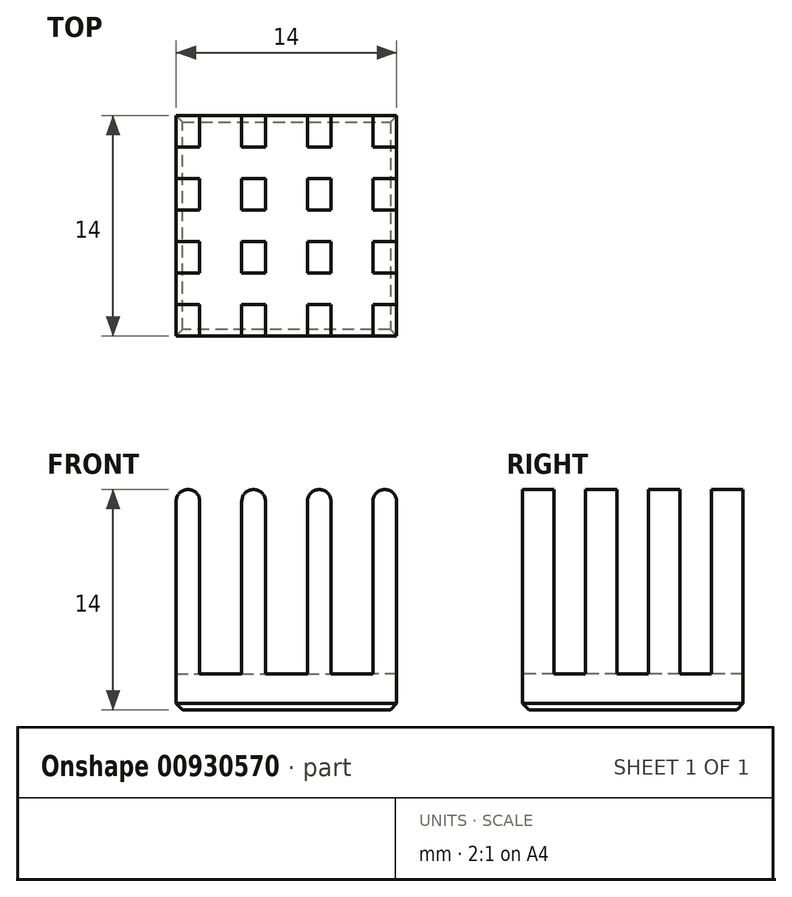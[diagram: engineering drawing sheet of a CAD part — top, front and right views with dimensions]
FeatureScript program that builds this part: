
annotation { "Feature Type Name" : "Feature", "Feature Type Description" : "" }
export const myFeature = defineFeature(function(context is Context, id is Id, definition is map)
    precondition{}
    {
        {
            var Q0;
            Q0=qCreatedBy(makeId("Top.planeOp"),FACE);
            var sketch = newSketch(context, id + "F0", { "sketchPlane" : qUnion([Q0])});
            skLineSegment(sketch, "E0.bottom", {"start": v(0, 0) * mm, "end": v(14, 0) * mm});
            skLineSegment(sketch, "E0.top", {"start": v(0, 14) * mm, "end": v(14, 14) * mm});
            skLineSegment(sketch, "E0.left", {"start": v(0, 0) * mm, "end": v(0, 14) * mm});
            skLineSegment(sketch, "E0.right", {"start": v(14, 0) * mm, "end": v(14, 14) * mm});
            skSolve(sketch);
        }
        {
            var Q0;
            Q0=qSketchRegion(id+"F0",true);
            extrude(context, id + "F1", {"entities" : qUnion([Q0]), "depth" : 2.3 * mm});
        }
        {
            var Q0;
            Q0=makeQuery(id+"F1.opExtrude","CAP_FACE",FACE,{"disambiguationData":[OSD([sQuery(id+"F0.wireOp",EDGE,"E0.bottom"),sQuery(id+"F0.wireOp",EDGE,"E0.top"),sQuery(id+"F0.wireOp",EDGE,"E0.left"),sQuery(id+"F0.wireOp",EDGE,"E0.right")])],"isStart":false});
            var sketch = newSketch(context, id + "F2", { "sketchPlane" : qUnion([Q0])});
            skLineSegment(sketch, "E1.bottom", {"start": v(0, 14) * mm, "end": v(1.5, 14) * mm});
            skLineSegment(sketch, "E1.top", {"start": v(0, 12) * mm, "end": v(1.5, 12) * mm});
            skLineSegment(sketch, "E1.left", {"start": v(0, 14) * mm, "end": v(0, 12) * mm});
            skLineSegment(sketch, "E1.right", {"start": v(1.5, 14) * mm, "end": v(1.5, 12) * mm});
            skLineSegment(sketch, "E2.bottom", {"start": v(0, 0) * mm, "end": v(1.5, 0) * mm});
            skLineSegment(sketch, "E2.top", {"start": v(0, 2) * mm, "end": v(1.5, 2) * mm});
            skLineSegment(sketch, "E2.left", {"start": v(0, 0) * mm, "end": v(0, 2) * mm});
            skLineSegment(sketch, "E2.right", {"start": v(1.5, 0) * mm, "end": v(1.5, 2) * mm});
            skLineSegment(sketch, "E3.bottom", {"start": v(14, 14) * mm, "end": v(12.5, 14) * mm});
            skLineSegment(sketch, "E3.top", {"start": v(14, 12) * mm, "end": v(12.5, 12) * mm});
            skLineSegment(sketch, "E3.left", {"start": v(14, 14) * mm, "end": v(14, 12) * mm});
            skLineSegment(sketch, "E3.right", {"start": v(12.5, 14) * mm, "end": v(12.5, 12) * mm});
            skLineSegment(sketch, "E4.bottom", {"start": v(14, 0) * mm, "end": v(12.5, 0) * mm});
            skLineSegment(sketch, "E4.top", {"start": v(14, 2) * mm, "end": v(12.5, 2) * mm});
            skLineSegment(sketch, "E4.left", {"start": v(14, 0) * mm, "end": v(14, 2) * mm});
            skLineSegment(sketch, "E4.right", {"start": v(12.5, 0) * mm, "end": v(12.5, 2) * mm});
            skLineSegment(sketch, "E5.bottom", {"start": v(0, 10) * mm, "end": v(1.5, 10) * mm});
            skLineSegment(sketch, "E5.top", {"start": v(0, 8) * mm, "end": v(1.5, 8) * mm});
            skLineSegment(sketch, "E5.left", {"start": v(0, 10) * mm, "end": v(0, 8) * mm});
            skLineSegment(sketch, "E5.right", {"start": v(1.5, 10) * mm, "end": v(1.5, 8) * mm});
            skLineSegment(sketch, "E6.bottom", {"start": v(0, 6) * mm, "end": v(1.5, 6) * mm});
            skLineSegment(sketch, "E6.top", {"start": v(0, 4) * mm, "end": v(1.5, 4) * mm});
            skLineSegment(sketch, "E6.left", {"start": v(0, 6) * mm, "end": v(0, 4) * mm});
            skLineSegment(sketch, "E6.right", {"start": v(1.5, 6) * mm, "end": v(1.5, 4) * mm});
            skLineSegment(sketch, "E7.bottom", {"start": v(14, 10) * mm, "end": v(12.5, 10) * mm});
            skLineSegment(sketch, "E7.top", {"start": v(14, 8) * mm, "end": v(12.5, 8) * mm});
            skLineSegment(sketch, "E7.left", {"start": v(14, 10) * mm, "end": v(14, 8) * mm});
            skLineSegment(sketch, "E7.right", {"start": v(12.5, 10) * mm, "end": v(12.5, 8) * mm});
            skLineSegment(sketch, "E8.bottom", {"start": v(14, 6) * mm, "end": v(12.5, 6) * mm});
            skLineSegment(sketch, "E8.top", {"start": v(14, 4) * mm, "end": v(12.5, 4) * mm});
            skLineSegment(sketch, "E8.left", {"start": v(14, 6) * mm, "end": v(14, 4) * mm});
            skLineSegment(sketch, "E8.right", {"start": v(12.5, 6) * mm, "end": v(12.5, 4) * mm});
            skLineSegment(sketch, "E9.bottom", {"start": v(4.17, 10) * mm, "end": v(5.67, 10) * mm});
            skLineSegment(sketch, "E9.top", {"start": v(4.17, 8) * mm, "end": v(5.67, 8) * mm});
            skLineSegment(sketch, "E9.left", {"start": v(4.17, 10) * mm, "end": v(4.17, 8) * mm});
            skLineSegment(sketch, "E9.right", {"start": v(5.67, 10) * mm, "end": v(5.67, 8) * mm});
            skLineSegment(sketch, "E10.bottom", {"start": v(8.33, 10) * mm, "end": v(9.83, 10) * mm});
            skLineSegment(sketch, "E10.top", {"start": v(8.33, 8) * mm, "end": v(9.83, 8) * mm});
            skLineSegment(sketch, "E10.left", {"start": v(8.33, 10) * mm, "end": v(8.33, 8) * mm});
            skLineSegment(sketch, "E10.right", {"start": v(9.83, 10) * mm, "end": v(9.83, 8) * mm});
            skLineSegment(sketch, "E11.bottom", {"start": v(4.17, 14) * mm, "end": v(5.67, 14) * mm});
            skLineSegment(sketch, "E11.top", {"start": v(4.17, 12) * mm, "end": v(5.67, 12) * mm});
            skLineSegment(sketch, "E11.left", {"start": v(4.17, 14) * mm, "end": v(4.17, 12) * mm});
            skLineSegment(sketch, "E11.right", {"start": v(5.67, 14) * mm, "end": v(5.67, 12) * mm});
            skLineSegment(sketch, "E12.bottom", {"start": v(8.33, 14) * mm, "end": v(9.83, 14) * mm});
            skLineSegment(sketch, "E12.top", {"start": v(8.33, 12) * mm, "end": v(9.83, 12) * mm});
            skLineSegment(sketch, "E12.left", {"start": v(8.33, 14) * mm, "end": v(8.33, 12) * mm});
            skLineSegment(sketch, "E12.right", {"start": v(9.83, 14) * mm, "end": v(9.83, 12) * mm});
            skLineSegment(sketch, "E13.bottom", {"start": v(4.17, 6) * mm, "end": v(5.67, 6) * mm});
            skLineSegment(sketch, "E13.top", {"start": v(4.17, 4) * mm, "end": v(5.67, 4) * mm});
            skLineSegment(sketch, "E13.left", {"start": v(4.17, 6) * mm, "end": v(4.17, 4) * mm});
            skLineSegment(sketch, "E13.right", {"start": v(5.67, 6) * mm, "end": v(5.67, 4) * mm});
            skLineSegment(sketch, "E14.bottom", {"start": v(8.33, 6) * mm, "end": v(9.83, 6) * mm});
            skLineSegment(sketch, "E14.top", {"start": v(8.33, 4) * mm, "end": v(9.83, 4) * mm});
            skLineSegment(sketch, "E14.left", {"start": v(8.33, 6) * mm, "end": v(8.33, 4) * mm});
            skLineSegment(sketch, "E14.right", {"start": v(9.83, 6) * mm, "end": v(9.83, 4) * mm});
            skLineSegment(sketch, "E15.bottom", {"start": v(4.17, 2) * mm, "end": v(5.67, 2) * mm});
            skLineSegment(sketch, "E15.top", {"start": v(4.17, 0) * mm, "end": v(5.67, 0) * mm});
            skLineSegment(sketch, "E15.left", {"start": v(4.17, 2) * mm, "end": v(4.17, 0) * mm});
            skLineSegment(sketch, "E15.right", {"start": v(5.67, 2) * mm, "end": v(5.67, 0) * mm});
            skLineSegment(sketch, "E16.bottom", {"start": v(8.33, 2) * mm, "end": v(9.83, 2) * mm});
            skLineSegment(sketch, "E16.top", {"start": v(8.33, 0) * mm, "end": v(9.83, 0) * mm});
            skLineSegment(sketch, "E16.left", {"start": v(8.33, 2) * mm, "end": v(8.33, 0) * mm});
            skLineSegment(sketch, "E16.right", {"start": v(9.83, 2) * mm, "end": v(9.83, 0) * mm});
            skSolve(sketch);
        }
        {
            var Q0;
            Q0=qSketchRegion(id+"F2",true);
            extrude(context, id + "F3", {"entities" : qUnion([Q0]), "operationType" : NewBodyOperationType.ADD, "depth" : 11.7 * mm});
        }
        {
            var Q0;
            Q0=makeQuery(id+"F1.opExtrude","CAP_EDGE",EDGE,{"disambiguationData":[OSD([sQuery(id+"F0.wireOp",EDGE,"E0.bottom")])],"isStart":true});
            var Q1;
            Q1=makeQuery(id+"F1.opExtrude","CAP_EDGE",EDGE,{"disambiguationData":[OSD([sQuery(id+"F0.wireOp",EDGE,"E0.left")])],"isStart":true});
            var Q2;
            Q2=makeQuery(id+"F1.opExtrude","CAP_EDGE",EDGE,{"disambiguationData":[OSD([sQuery(id+"F0.wireOp",EDGE,"E0.right")])],"isStart":true});
            var Q3;
            Q3=makeQuery(id+"F1.opExtrude","CAP_EDGE",EDGE,{"disambiguationData":[OSD([sQuery(id+"F0.wireOp",EDGE,"E0.top")])],"isStart":true});
            chamfer(context, id + "F4", {"entities" : qUnion([Q0, Q1, Q2, Q3]), "width" : 0.4 * mm, "tangentPropagation" : true});
        }
        {
            var Q0;
            Q0=makeQuery(id+"F3.opExtrude","CAP_EDGE",EDGE,{"disambiguationData":[OSD([sQuery(id+"F2.wireOp",EDGE,"E3.left")])],"isStart":false});
            var Q1;
            Q1=makeQuery(id+"F3.opExtrude","CAP_EDGE",EDGE,{"disambiguationData":[OSD([sQuery(id+"F2.wireOp",EDGE,"E3.right")])],"isStart":false});
            var Q2;
            Q2=makeQuery(id+"F3.opExtrude","CAP_EDGE",EDGE,{"disambiguationData":[OSD([sQuery(id+"F2.wireOp",EDGE,"E12.right")])],"isStart":false});
            var Q3;
            Q3=makeQuery(id+"F3.opExtrude","CAP_EDGE",EDGE,{"disambiguationData":[OSD([sQuery(id+"F2.wireOp",EDGE,"E12.left")])],"isStart":false});
            var Q4;
            Q4=makeQuery(id+"F3.opExtrude","CAP_EDGE",EDGE,{"disambiguationData":[OSD([sQuery(id+"F2.wireOp",EDGE,"E11.right")])],"isStart":false});
            var Q5;
            Q5=makeQuery(id+"F3.opExtrude","CAP_EDGE",EDGE,{"disambiguationData":[OSD([sQuery(id+"F2.wireOp",EDGE,"E11.left")])],"isStart":false});
            var Q6;
            Q6=makeQuery(id+"F3.opExtrude","CAP_EDGE",EDGE,{"disambiguationData":[OSD([sQuery(id+"F2.wireOp",EDGE,"E1.right")])],"isStart":false});
            var Q7;
            Q7=makeQuery(id+"F3.opExtrude","CAP_EDGE",EDGE,{"disambiguationData":[OSD([sQuery(id+"F2.wireOp",EDGE,"E1.left")])],"isStart":false});
            var Q8;
            Q8=makeQuery(id+"F3.opExtrude","CAP_EDGE",EDGE,{"disambiguationData":[OSD([sQuery(id+"F2.wireOp",EDGE,"E5.left")])],"isStart":false});
            var Q9;
            Q9=makeQuery(id+"F3.opExtrude","CAP_EDGE",EDGE,{"disambiguationData":[OSD([sQuery(id+"F2.wireOp",EDGE,"E5.right")])],"isStart":false});
            var Q10;
            Q10=makeQuery(id+"F3.opExtrude","CAP_EDGE",EDGE,{"disambiguationData":[OSD([sQuery(id+"F2.wireOp",EDGE,"E9.left")])],"isStart":false});
            var Q11;
            Q11=makeQuery(id+"F3.opExtrude","CAP_EDGE",EDGE,{"disambiguationData":[OSD([sQuery(id+"F2.wireOp",EDGE,"E9.right")])],"isStart":false});
            var Q12;
            Q12=makeQuery(id+"F3.opExtrude","CAP_EDGE",EDGE,{"disambiguationData":[OSD([sQuery(id+"F2.wireOp",EDGE,"E10.left")])],"isStart":false});
            var Q13;
            Q13=makeQuery(id+"F3.opExtrude","CAP_EDGE",EDGE,{"disambiguationData":[OSD([sQuery(id+"F2.wireOp",EDGE,"E10.right")])],"isStart":false});
            var Q14;
            Q14=makeQuery(id+"F3.opExtrude","CAP_EDGE",EDGE,{"disambiguationData":[OSD([sQuery(id+"F2.wireOp",EDGE,"E7.right")])],"isStart":false});
            var Q15;
            Q15=makeQuery(id+"F3.opExtrude","CAP_EDGE",EDGE,{"disambiguationData":[OSD([sQuery(id+"F2.wireOp",EDGE,"E7.left")])],"isStart":false});
            var Q16;
            Q16=makeQuery(id+"F3.opExtrude","CAP_EDGE",EDGE,{"disambiguationData":[OSD([sQuery(id+"F2.wireOp",EDGE,"E8.left")])],"isStart":false});
            var Q17;
            Q17=makeQuery(id+"F3.opExtrude","CAP_EDGE",EDGE,{"disambiguationData":[OSD([sQuery(id+"F2.wireOp",EDGE,"E8.right")])],"isStart":false});
            var Q18;
            Q18=makeQuery(id+"F3.opExtrude","CAP_EDGE",EDGE,{"disambiguationData":[OSD([sQuery(id+"F2.wireOp",EDGE,"E14.right")])],"isStart":false});
            var Q19;
            Q19=makeQuery(id+"F3.opExtrude","CAP_EDGE",EDGE,{"disambiguationData":[OSD([sQuery(id+"F2.wireOp",EDGE,"E14.left")])],"isStart":false});
            var Q20;
            Q20=makeQuery(id+"F3.opExtrude","CAP_EDGE",EDGE,{"disambiguationData":[OSD([sQuery(id+"F2.wireOp",EDGE,"E13.right")])],"isStart":false});
            var Q21;
            Q21=makeQuery(id+"F3.opExtrude","CAP_EDGE",EDGE,{"disambiguationData":[OSD([sQuery(id+"F2.wireOp",EDGE,"E13.left")])],"isStart":false});
            var Q22;
            Q22=makeQuery(id+"F3.opExtrude","CAP_EDGE",EDGE,{"disambiguationData":[OSD([sQuery(id+"F2.wireOp",EDGE,"E6.right")])],"isStart":false});
            var Q23;
            Q23=makeQuery(id+"F3.opExtrude","CAP_EDGE",EDGE,{"disambiguationData":[OSD([sQuery(id+"F2.wireOp",EDGE,"E6.left")])],"isStart":false});
            var Q24;
            Q24=makeQuery(id+"F3.opExtrude","CAP_EDGE",EDGE,{"disambiguationData":[OSD([sQuery(id+"F2.wireOp",EDGE,"E2.left")])],"isStart":false});
            var Q25;
            Q25=makeQuery(id+"F3.opExtrude","CAP_EDGE",EDGE,{"disambiguationData":[OSD([sQuery(id+"F2.wireOp",EDGE,"E2.right")])],"isStart":false});
            var Q26;
            Q26=makeQuery(id+"F3.opExtrude","CAP_EDGE",EDGE,{"disambiguationData":[OSD([sQuery(id+"F2.wireOp",EDGE,"E15.left")])],"isStart":false});
            var Q27;
            Q27=makeQuery(id+"F3.opExtrude","CAP_EDGE",EDGE,{"disambiguationData":[OSD([sQuery(id+"F2.wireOp",EDGE,"E15.right")])],"isStart":false});
            var Q28;
            Q28=makeQuery(id+"F3.opExtrude","CAP_EDGE",EDGE,{"disambiguationData":[OSD([sQuery(id+"F2.wireOp",EDGE,"E16.left")])],"isStart":false});
            var Q29;
            Q29=makeQuery(id+"F3.opExtrude","CAP_EDGE",EDGE,{"disambiguationData":[OSD([sQuery(id+"F2.wireOp",EDGE,"E16.right")])],"isStart":false});
            var Q30;
            Q30=makeQuery(id+"F3.opExtrude","CAP_EDGE",EDGE,{"disambiguationData":[OSD([sQuery(id+"F2.wireOp",EDGE,"E4.right")])],"isStart":false});
            var Q31;
            Q31=makeQuery(id+"F3.opExtrude","CAP_EDGE",EDGE,{"disambiguationData":[OSD([sQuery(id+"F2.wireOp",EDGE,"E4.left")])],"isStart":false});
            fillet(context, id + "F5", {"entities" : qUnion([Q0, Q1, Q2, Q3, Q4, Q5, Q6, Q7, Q8, Q9, Q10, Q11, Q12, Q13, Q14, Q15, Q16, Q17, Q18, Q19, Q20, Q21, Q22, Q23, Q24, Q25, Q26, Q27, Q28, Q29, Q30, Q31]), "radius" : 0.75 * mm, "tangentPropagation" : true, "allowEdgeOverflow" : false});
        }
    });
